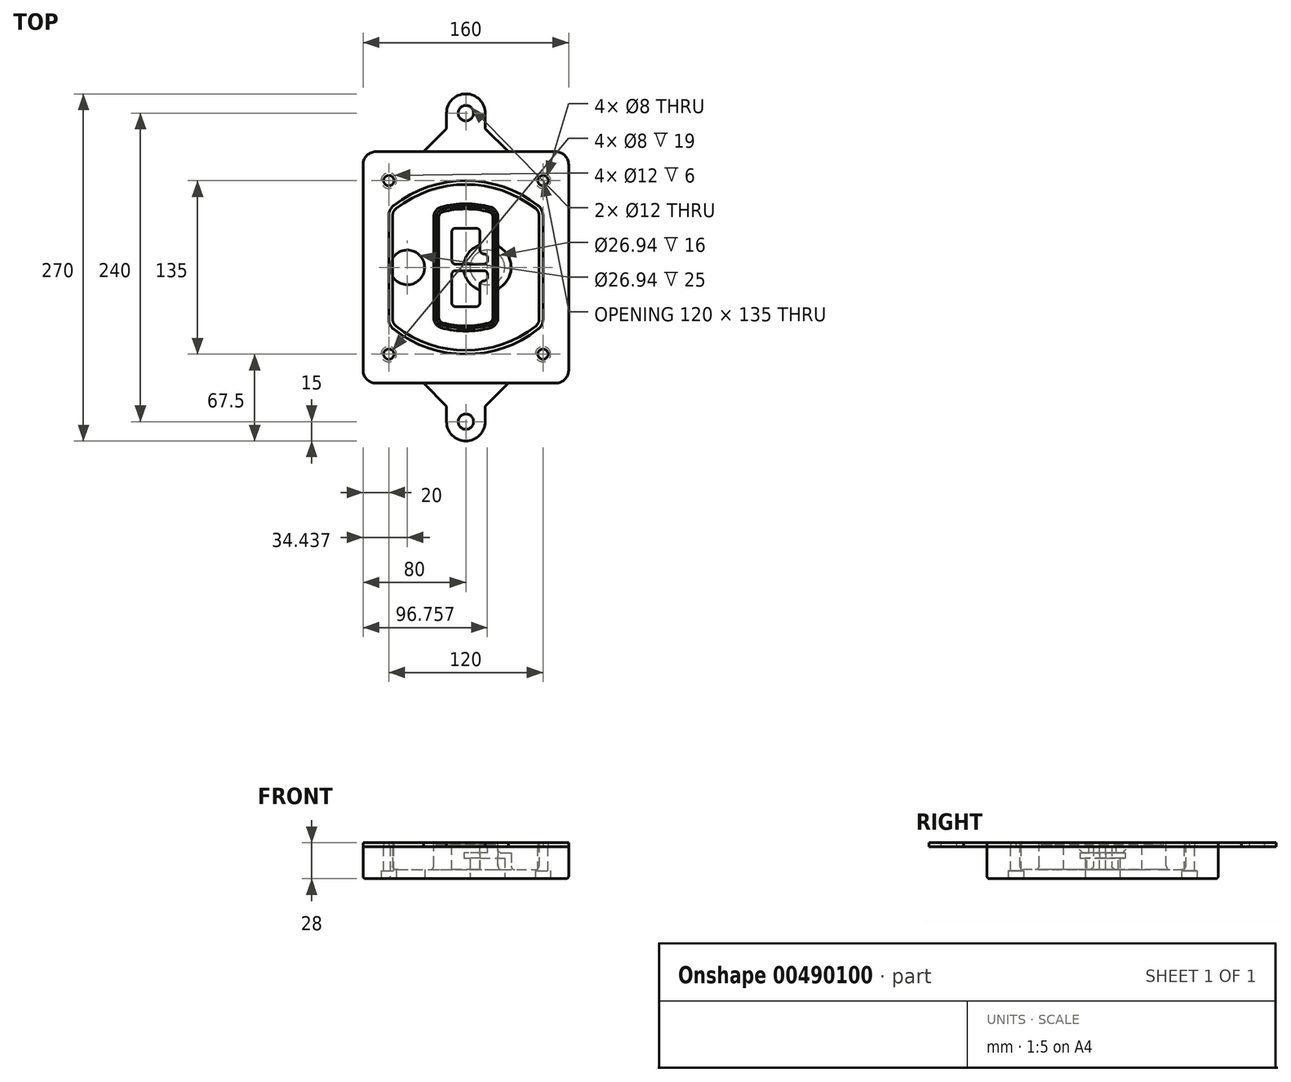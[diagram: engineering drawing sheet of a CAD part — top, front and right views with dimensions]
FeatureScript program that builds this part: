
annotation { "Feature Type Name" : "Feature", "Feature Type Description" : "" }
export const myFeature = defineFeature(function(context is Context, id is Id, definition is map)
    precondition{}
    {
        {
            var Q0;
            Q0=qCreatedBy(makeId("Top.planeOp"),FACE);
            var sketch = newSketch(context, id + "F0", { "sketchPlane" : qUnion([Q0])});
            skPoint(sketch, "E0.rect.middle", {"position": v(0, 0) * mm});
            skLineSegment(sketch, "E1.bottom", {"start": v(-70, -90) * mm, "end": v(70, -90) * mm});
            skLineSegment(sketch, "E1.top", {"start": v(-70, 90) * mm, "end": v(70, 90) * mm});
            skLineSegment(sketch, "E1.left", {"start": v(-80, -80) * mm, "end": v(-80, 80) * mm});
            skLineSegment(sketch, "E1.right", {"start": v(80, -80) * mm, "end": v(80, 80) * mm});
            skLineSegment(sketch, "E2", {"start": v(-80, 90) * mm, "end": v(80, -90) * mm, "construction": true});
            skLineSegment(sketch, "E3", {"start": v(80, 90) * mm, "end": v(-80, -90) * mm, "construction": true});
            skCircle(sketch, "E4", {"center": v(-60, 67.5) * mm, "radius": 4 * mm});
            skCircle(sketch, "E5", {"center": v(60, 67.5) * mm, "radius": 4 * mm});
            skCircle(sketch, "E6", {"center": v(60, -67.5) * mm, "radius": 4 * mm});
            skCircle(sketch, "E7", {"center": v(-60, -67.5) * mm, "radius": 4 * mm});
            skLineSegment(sketch, "E8", {"start": v(-60, 67.5) * mm, "end": v(60, 67.5) * mm, "construction": true});
            skLineSegment(sketch, "E9", {"start": v(60, 67.5) * mm, "end": v(60, -67.5) * mm, "construction": true});
            skLineSegment(sketch, "E10", {"start": v(60, -67.5) * mm, "end": v(-60, -67.5) * mm, "construction": true});
            skLineSegment(sketch, "E11", {"start": v(-60, -67.5) * mm, "end": v(-60, 67.5) * mm, "construction": true});
            skLineSegment(sketch, "E12", {"start": v(-60, 40.3) * mm, "end": v(-60, -40.3) * mm});
            skLineSegment(sketch, "E13", {"start": v(60, 40.3) * mm, "end": v(60, -40.3) * mm});
            skArc(sketch, "E14", {"start": v(56.15, 48.18) * mm, "mid": v(0, 67.5) * mm, "end": v(-56.15, 48.18) * mm});
            skArc(sketch, "E15", {"start": v(-56.15, -48.18) * mm, "mid": v(0, -67.5) * mm, "end": v(56.15, -48.18) * mm});
            skLineSegment(sketch, "E16", {"start": v(-60, 0) * mm, "end": v(60, 0) * mm, "construction": true});
            skPoint(sketch, "E17.visualSharp", {"position": v(-60, -45) * mm});
            skArc(sketch, "E17.filletArc", {"start": v(-60, -40.3) * mm, "mid": v(-58.99, -44.68) * mm, "end": v(-56.15, -48.18) * mm});
            skPoint(sketch, "E18.visualSharp", {"position": v(-60, 45) * mm});
            skArc(sketch, "E18.filletArc", {"start": v(-56.15, 48.18) * mm, "mid": v(-58.99, 44.68) * mm, "end": v(-60, 40.3) * mm});
            skPoint(sketch, "E19.visualSharp", {"position": v(60, 45) * mm});
            skArc(sketch, "E19.filletArc", {"start": v(60, 40.3) * mm, "mid": v(58.99, 44.68) * mm, "end": v(56.15, 48.18) * mm});
            skPoint(sketch, "E20.visualSharp", {"position": v(60, -45) * mm});
            skArc(sketch, "E20.filletArc", {"start": v(56.15, -48.18) * mm, "mid": v(58.99, -44.68) * mm, "end": v(60, -40.3) * mm});
            skPoint(sketch, "E21.visualSharp", {"position": v(-80, 90) * mm});
            skArc(sketch, "E21.filletArc", {"start": v(-70, 90) * mm, "mid": v(-77.07, 87.07) * mm, "end": v(-80, 80) * mm});
            skPoint(sketch, "E22.visualSharp", {"position": v(80, 90) * mm});
            skArc(sketch, "E22.filletArc", {"start": v(80, 80) * mm, "mid": v(77.07, 87.07) * mm, "end": v(70, 90) * mm});
            skPoint(sketch, "E23.visualSharp", {"position": v(80, -90) * mm});
            skArc(sketch, "E23.filletArc", {"start": v(70, -90) * mm, "mid": v(77.07, -87.07) * mm, "end": v(80, -80) * mm});
            skPoint(sketch, "E24.visualSharp", {"position": v(-80, -90) * mm});
            skArc(sketch, "E24.filletArc", {"start": v(-80, -80) * mm, "mid": v(-77.07, -87.07) * mm, "end": v(-70, -90) * mm});
            skArc(sketch, "E25.0", {"start": v(57, 40.3) * mm, "mid": v(56.3, 43.36) * mm, "end": v(54.3, 45.81) * mm});
            skLineSegment(sketch, "E25.1", {"start": v(57, 40.3) * mm, "end": v(57, -40.3) * mm});
            skArc(sketch, "E25.2", {"start": v(54.3, -45.81) * mm, "mid": v(56.3, -43.36) * mm, "end": v(57, -40.3) * mm});
            skArc(sketch, "E25.3", {"start": v(-54.3, -45.81) * mm, "mid": v(0, -64.5) * mm, "end": v(54.3, -45.81) * mm});
            skArc(sketch, "E25.4", {"start": v(-57, -40.3) * mm, "mid": v(-56.3, -43.36) * mm, "end": v(-54.3, -45.81) * mm});
            skArc(sketch, "E25.5", {"start": v(54.3, 45.81) * mm, "mid": v(0, 64.5) * mm, "end": v(-54.3, 45.81) * mm});
            skLineSegment(sketch, "E25.6", {"start": v(-57, 40.3) * mm, "end": v(-57, -40.3) * mm});
            skArc(sketch, "E25.7", {"start": v(-54.3, 45.81) * mm, "mid": v(-56.3, 43.36) * mm, "end": v(-57, 40.3) * mm});
            skArc(sketch, "E26.0", {"start": v(-58.62, 51.33) * mm, "mid": v(-62.58, 46.43) * mm, "end": v(-64, 40.3) * mm});
            skArc(sketch, "E26.1", {"start": v(58.62, 51.33) * mm, "mid": v(0, 71.5) * mm, "end": v(-58.62, 51.33) * mm});
            skArc(sketch, "E26.2", {"start": v(64, 40.3) * mm, "mid": v(62.58, 46.43) * mm, "end": v(58.62, 51.33) * mm});
            skLineSegment(sketch, "E26.3", {"start": v(64, 40.3) * mm, "end": v(64, -40.3) * mm});
            skArc(sketch, "E26.4", {"start": v(58.62, -51.33) * mm, "mid": v(62.58, -46.43) * mm, "end": v(64, -40.3) * mm});
            skLineSegment(sketch, "E26.5", {"start": v(-64, 40.3) * mm, "end": v(-64, -40.3) * mm});
            skArc(sketch, "E26.6", {"start": v(-58.62, -51.33) * mm, "mid": v(0, -71.5) * mm, "end": v(58.62, -51.33) * mm});
            skArc(sketch, "E26.7", {"start": v(-64, -40.3) * mm, "mid": v(-62.58, -46.43) * mm, "end": v(-58.62, -51.33) * mm});
            skSolve(sketch);
        }
        {
            var Q0;
            Q0=makeQuery(id+"F0.imprint","IMPRINT",FACE,{"disambiguationData":[TD([[makeQuery(id+"F0.imprint","IMPRINT",EDGE,{"derivedFrom":sQuery(id+"F0.wireOp",EDGE,"E1.bottom")}),1.0]])]});
            var Q1;
            Q1=makeQuery(id+"F0.imprint","IMPRINT",FACE,{"disambiguationData":[TD([[makeQuery(id+"F0.imprint","IMPRINT",EDGE,{"derivedFrom":sQuery(id+"F0.wireOp",EDGE,"E12")}),1.0]])]});
            var Q2;
            Q2=makeQuery(id+"F0.imprint","IMPRINT",FACE,{"disambiguationData":[TD([[makeQuery(id+"F0.imprint","IMPRINT",EDGE,{"derivedFrom":sQuery(id+"F0.wireOp",EDGE,"E25.0")}),1.0]])]});
            var Q3;
            Q3=makeQuery(id+"F0.imprint","IMPRINT",FACE,{"disambiguationData":[TD([[makeQuery(id+"F0.imprint","IMPRINT",EDGE,{"derivedFrom":sQuery(id+"F0.wireOp",EDGE,"E12")}),-1.0]])]});
            extrude(context, id + "F1", {"entities" : qUnion([Q0, Q1, Q2, Q3]), "oppositeDirection" : true, "depth" : 25 * mm});
        }
        {
            var Q0;
            Q0=makeQuery(id+"F0.imprint","IMPRINT",FACE,{"disambiguationData":[TD([[makeQuery(id+"F0.imprint","IMPRINT",EDGE,{"derivedFrom":sQuery(id+"F0.wireOp",EDGE,"E12")}),1.0]])]});
            extrude(context, id + "F2", {"entities" : qUnion([Q0]), "operationType" : NewBodyOperationType.ADD, "depth" : 3 * mm});
        }
        {
            var Q0;
            Q0=makeQuery(id+"F0.imprint","IMPRINT",FACE,{"disambiguationData":[TD([[makeQuery(id+"F0.imprint","IMPRINT",EDGE,{"derivedFrom":sQuery(id+"F0.wireOp",EDGE,"E25.0")}),1.0]])]});
            extrude(context, id + "F3", {"entities" : qUnion([Q0]), "operationType" : NewBodyOperationType.REMOVE, "oppositeDirection" : true, "depth" : 18 * mm});
        }
        {
            var Q0;
            Q0=makeQuery(id+"F2.opExtrude","CAP_FACE",FACE,{"disambiguationData":[OSD([sQuery(id+"F0.wireOp",EDGE,"E12"),sQuery(id+"F0.wireOp",EDGE,"E13"),sQuery(id+"F0.wireOp",EDGE,"E14"),sQuery(id+"F0.wireOp",EDGE,"E15"),sQuery(id+"F0.wireOp",EDGE,"E17.filletArc"),sQuery(id+"F0.wireOp",EDGE,"E18.filletArc"),sQuery(id+"F0.wireOp",EDGE,"E19.filletArc"),sQuery(id+"F0.wireOp",EDGE,"E20.filletArc"),sQuery(id+"F0.wireOp",EDGE,"E25.0"),sQuery(id+"F0.wireOp",EDGE,"E25.1"),sQuery(id+"F0.wireOp",EDGE,"E25.2"),sQuery(id+"F0.wireOp",EDGE,"E25.3"),sQuery(id+"F0.wireOp",EDGE,"E25.4"),sQuery(id+"F0.wireOp",EDGE,"E25.5"),sQuery(id+"F0.wireOp",EDGE,"E25.6"),sQuery(id+"F0.wireOp",EDGE,"E25.7")])],"isStart":false});
            var sketch = newSketch(context, id + "F4", { "sketchPlane" : qUnion([Q0])});
            skArc(sketch, "E27.0", {"start": v(-19.08, -46.97) * mm, "mid": v(0, -49.5) * mm, "end": v(19.08, -46.97) * mm});
            skArc(sketch, "E28.0", {"start": v(19.08, 46.97) * mm, "mid": v(0, 49.5) * mm, "end": v(-19.08, 46.97) * mm});
            skLineSegment(sketch, "E29", {"start": v(-25, 39.25) * mm, "end": v(-25, -39.25) * mm});
            skLineSegment(sketch, "E30", {"start": v(25, 39.25) * mm, "end": v(25, -39.25) * mm});
            skLineSegment(sketch, "E31", {"start": v(-25, 45.1) * mm, "end": v(25, 45.1) * mm, "construction": true});
            skLineSegment(sketch, "E32", {"start": v(-25, -45.1) * mm, "end": v(25, -45.1) * mm, "construction": true});
            skPoint(sketch, "E33.visualSharp", {"position": v(-25, 45.1) * mm});
            skArc(sketch, "E33.filletArc", {"start": v(-19.08, 46.97) * mm, "mid": v(-23.35, 44.11) * mm, "end": v(-25, 39.25) * mm});
            skPoint(sketch, "E34.visualSharp", {"position": v(25, 45.1) * mm});
            skArc(sketch, "E34.filletArc", {"start": v(25, 39.25) * mm, "mid": v(23.35, 44.11) * mm, "end": v(19.08, 46.97) * mm});
            skPoint(sketch, "E35.visualSharp", {"position": v(25, -45.1) * mm});
            skArc(sketch, "E35.filletArc", {"start": v(19.08, -46.97) * mm, "mid": v(23.35, -44.11) * mm, "end": v(25, -39.25) * mm});
            skPoint(sketch, "E36.visualSharp", {"position": v(-25, -45.1) * mm});
            skArc(sketch, "E36.filletArc", {"start": v(-25, -39.25) * mm, "mid": v(-23.35, -44.11) * mm, "end": v(-19.08, -46.97) * mm});
            skArc(sketch, "E37.0", {"start": v(54.3, 45.81) * mm, "mid": v(0, 64.5) * mm, "end": v(-54.3, 45.81) * mm});
            skArc(sketch, "E37.1", {"start": v(-54.3, 45.81) * mm, "mid": v(-56.3, 43.36) * mm, "end": v(-57, 40.3) * mm});
            skLineSegment(sketch, "E37.2", {"start": v(-57, 40.3) * mm, "end": v(-57, -40.3) * mm});
            skArc(sketch, "E37.3", {"start": v(-57, -40.3) * mm, "mid": v(-56.3, -43.36) * mm, "end": v(-54.3, -45.81) * mm});
            skArc(sketch, "E37.4", {"start": v(-54.3, -45.81) * mm, "mid": v(0, -64.5) * mm, "end": v(54.3, -45.81) * mm});
            skArc(sketch, "E37.5", {"start": v(54.3, -45.81) * mm, "mid": v(56.3, -43.36) * mm, "end": v(57, -40.3) * mm});
            skLineSegment(sketch, "E37.6", {"start": v(57, 40.3) * mm, "end": v(57, -40.3) * mm});
            skArc(sketch, "E37.7", {"start": v(57, 40.3) * mm, "mid": v(56.3, 43.36) * mm, "end": v(54.3, 45.81) * mm});
            skLineSegment(sketch, "E38.0", {"start": v(23, 39.25) * mm, "end": v(23, -39.25) * mm});
            skArc(sketch, "E38.1", {"start": v(18.56, -45.04) * mm, "mid": v(21.76, -42.9) * mm, "end": v(23, -39.25) * mm});
            skArc(sketch, "E38.2", {"start": v(-18.56, -45.04) * mm, "mid": v(0, -47.5) * mm, "end": v(18.56, -45.04) * mm});
            skArc(sketch, "E38.3", {"start": v(-23, -39.25) * mm, "mid": v(-21.76, -42.9) * mm, "end": v(-18.56, -45.04) * mm});
            skLineSegment(sketch, "E38.4", {"start": v(-23, 39.25) * mm, "end": v(-23, -39.25) * mm});
            skArc(sketch, "E38.5", {"start": v(23, 39.25) * mm, "mid": v(21.76, 42.9) * mm, "end": v(18.56, 45.04) * mm});
            skArc(sketch, "E38.6", {"start": v(-18.56, 45.04) * mm, "mid": v(-21.76, 42.9) * mm, "end": v(-23, 39.25) * mm});
            skArc(sketch, "E38.7", {"start": v(18.56, 45.04) * mm, "mid": v(0, 47.5) * mm, "end": v(-18.56, 45.04) * mm});
            skArc(sketch, "E39.0", {"start": v(21, 39.25) * mm, "mid": v(20.18, 41.68) * mm, "end": v(18.04, 43.1) * mm});
            skLineSegment(sketch, "E39.1", {"start": v(21, 39.25) * mm, "end": v(21, -39.25) * mm});
            skArc(sketch, "E39.2", {"start": v(18.04, -43.1) * mm, "mid": v(20.18, -41.68) * mm, "end": v(21, -39.25) * mm});
            skArc(sketch, "E39.3", {"start": v(-18.04, -43.1) * mm, "mid": v(0, -45.5) * mm, "end": v(18.04, -43.1) * mm});
            skArc(sketch, "E39.4", {"start": v(-21, -39.25) * mm, "mid": v(-20.18, -41.68) * mm, "end": v(-18.04, -43.1) * mm});
            skArc(sketch, "E39.5", {"start": v(18.04, 43.1) * mm, "mid": v(0, 45.5) * mm, "end": v(-18.04, 43.1) * mm});
            skLineSegment(sketch, "E39.6", {"start": v(-21, 39.25) * mm, "end": v(-21, -39.25) * mm});
            skArc(sketch, "E39.7", {"start": v(-18.04, 43.1) * mm, "mid": v(-20.18, 41.68) * mm, "end": v(-21, 39.25) * mm});
            skLineSegment(sketch, "E40", {"start": v(-25, 0) * mm, "end": v(25, 0) * mm, "construction": true});
            skLineSegment(sketch, "E41", {"start": v(-11, 5.5) * mm, "end": v(-11, 27.5) * mm});
            skLineSegment(sketch, "E42", {"start": v(-8, 30.5) * mm, "end": v(8, 30.5) * mm});
            skLineSegment(sketch, "E43", {"start": v(11, 27.5) * mm, "end": v(11, 13.5) * mm});
            skLineSegment(sketch, "E44", {"start": v(14, 10.5) * mm, "end": v(14, 10.5) * mm});
            skLineSegment(sketch, "E45", {"start": v(17, 7.5) * mm, "end": v(17, 5.5) * mm});
            skLineSegment(sketch, "E46", {"start": v(14, 2.5) * mm, "end": v(-8, 2.5) * mm});
            skPoint(sketch, "E47.visualSharp", {"position": v(-11, 30.5) * mm});
            skArc(sketch, "E47.filletArc", {"start": v(-8, 30.5) * mm, "mid": v(-10.12, 29.62) * mm, "end": v(-11, 27.5) * mm});
            skPoint(sketch, "E48.visualSharp", {"position": v(11, 30.5) * mm});
            skArc(sketch, "E48.filletArc", {"start": v(11, 27.5) * mm, "mid": v(10.12, 29.62) * mm, "end": v(8, 30.5) * mm});
            skPoint(sketch, "E49.visualSharp", {"position": v(11, 10.5) * mm});
            skArc(sketch, "E49.filletArc", {"start": v(11, 13.5) * mm, "mid": v(11.88, 11.38) * mm, "end": v(14, 10.5) * mm});
            skPoint(sketch, "E50.visualSharp", {"position": v(17, 10.5) * mm});
            skArc(sketch, "E50.filletArc", {"start": v(17, 7.5) * mm, "mid": v(16.12, 9.62) * mm, "end": v(14, 10.5) * mm});
            skPoint(sketch, "E51.visualSharp", {"position": v(17, 2.5) * mm});
            skArc(sketch, "E51.filletArc", {"start": v(14, 2.5) * mm, "mid": v(16.12, 3.38) * mm, "end": v(17, 5.5) * mm});
            skPoint(sketch, "E52.visualSharp", {"position": v(-11, 2.5) * mm});
            skArc(sketch, "E52.filletArc", {"start": v(-11, 5.5) * mm, "mid": v(-10.12, 3.38) * mm, "end": v(-8, 2.5) * mm});
            skLineSegment(sketch, "E53.0.MirrorCS", {"start": v(14, -2.5) * mm, "end": v(-8, -2.5) * mm});
            skArc(sketch, "E54.0.MirrorCS", {"start": v(-11, -5.5) * mm, "mid": v(-10.12, -3.38) * mm, "end": v(-8, -2.5) * mm});
            skLineSegment(sketch, "E55.0.MirrorCS", {"start": v(-11, -5.5) * mm, "end": v(-11, -27.5) * mm});
            skArc(sketch, "E56.0.MirrorCS", {"start": v(-8, -30.5) * mm, "mid": v(-10.12, -29.62) * mm, "end": v(-11, -27.5) * mm});
            skLineSegment(sketch, "E57.0.MirrorCS", {"start": v(-8, -30.5) * mm, "end": v(8, -30.5) * mm});
            skArc(sketch, "E58.0.MirrorCS", {"start": v(11, -27.5) * mm, "mid": v(10.12, -29.62) * mm, "end": v(8, -30.5) * mm});
            skLineSegment(sketch, "E59.0.MirrorCS", {"start": v(11, -27.5) * mm, "end": v(11, -13.5) * mm});
            skArc(sketch, "E60.0.MirrorCS", {"start": v(11, -13.5) * mm, "mid": v(11.88, -11.38) * mm, "end": v(14, -10.5) * mm});
            skArc(sketch, "E61.0.MirrorCS", {"start": v(17, -7.5) * mm, "mid": v(16.12, -9.62) * mm, "end": v(14, -10.5) * mm});
            skLineSegment(sketch, "E62.0.MirrorCS", {"start": v(17, -7.5) * mm, "end": v(17, -5.5) * mm});
            skArc(sketch, "E63.0.MirrorCS", {"start": v(14, -2.5) * mm, "mid": v(16.12, -3.38) * mm, "end": v(17, -5.5) * mm});
            skSolve(sketch);
        }
        {
            var Q0;
            Q0=makeQuery(id+"F4.imprint","IMPRINT",FACE,{"disambiguationData":[TD([[makeQuery(id+"F4.imprint","IMPRINT",EDGE,{"derivedFrom":sQuery(id+"F4.wireOp",EDGE,"E27.0")}),1.0]])]});
            var Q1;
            Q1=makeQuery(id+"F4.imprint","IMPRINT",FACE,{"disambiguationData":[TD([[makeQuery(id+"F4.imprint","IMPRINT",EDGE,{"derivedFrom":sQuery(id+"F4.wireOp",EDGE,"E38.0")}),-1.0]])]});
            var Q2;
            Q2=makeQuery(id+"F4.imprint","IMPRINT",FACE,{"disambiguationData":[TD([[makeQuery(id+"F4.imprint","IMPRINT",EDGE,{"derivedFrom":sQuery(id+"F4.wireOp",EDGE,"E39.0")}),1.0]])]});
            extrude(context, id + "F5", {"entities" : qUnion([Q0, Q1, Q2]), "operationType" : NewBodyOperationType.ADD, "endBound" : BoundingType.UP_TO_NEXT, "oppositeDirection" : true, "depth" : 25 * mm});
        }
        {
            var Q0;
            Q0=makeQuery(id+"F4.imprint","IMPRINT",FACE,{"disambiguationData":[TD([[makeQuery(id+"F4.imprint","IMPRINT",EDGE,{"derivedFrom":sQuery(id+"F4.wireOp",EDGE,"E38.0")}),-1.0]])]});
            extrude(context, id + "F6", {"entities" : qUnion([Q0]), "operationType" : NewBodyOperationType.REMOVE, "oppositeDirection" : true, "depth" : 2 * mm});
        }
        {
            var Q0;
            Q0=makeQuery(id+"F1.opExtrude","CAP_FACE",FACE,{"disambiguationData":[OSD([sQuery(id+"F0.wireOp",EDGE,"E1.bottom"),sQuery(id+"F0.wireOp",EDGE,"E1.top"),sQuery(id+"F0.wireOp",EDGE,"E1.left"),sQuery(id+"F0.wireOp",EDGE,"E1.right"),sQuery(id+"F0.wireOp",EDGE,"E4"),sQuery(id+"F0.wireOp",EDGE,"E5"),sQuery(id+"F0.wireOp",EDGE,"E6"),sQuery(id+"F0.wireOp",EDGE,"E7"),sQuery(id+"F0.wireOp",EDGE,"E21.filletArc"),sQuery(id+"F0.wireOp",EDGE,"E22.filletArc"),sQuery(id+"F0.wireOp",EDGE,"E23.filletArc"),sQuery(id+"F0.wireOp",EDGE,"E24.filletArc")])],"isStart":false});
            var sketch = newSketch(context, id + "F7", { "sketchPlane" : qUnion([Q0])});
            skCircle(sketch, "E64", {"center": v(16.76, 0) * mm, "radius": 13.47 * mm});
            skCircle(sketch, "E65", {"center": v(-45.56, 0) * mm, "radius": 13.47 * mm});
            skLineSegment(sketch, "E66", {"start": v(80, 0) * mm, "end": v(-80, 0) * mm});
            skCircle(sketch, "E67", {"center": v(16.76, 0) * mm, "radius": 18.47 * mm});
            skCircle(sketch, "E68", {"center": v(60, -67.5) * mm, "radius": 6 * mm});
            skCircle(sketch, "E69", {"center": v(-60, -67.5) * mm, "radius": 6 * mm});
            skCircle(sketch, "E70", {"center": v(-60, 67.5) * mm, "radius": 6 * mm});
            skCircle(sketch, "E71", {"center": v(60, 67.5) * mm, "radius": 6 * mm});
            skSolve(sketch);
        }
        {
            var Q0;
            {var subQ1=sQuery(id+"F7.wireOp",EDGE,"E66");var subQ4=sQuery(id+"F7.wireOp",EDGE,"E64");var subQ6=makeQuery(id+"F7.imprint","INTERSECT",VERTEX,{"disambiguationData":[OD(0.0)],"derivedFrom":[subQ4,subQ1]});Q0=makeQuery(id+"F7.imprint","IMPRINT",FACE,{"disambiguationData":[TD([[makeQuery(id+"F7.imprint","IMPRINT",EDGE,{"disambiguationData":[TD([[subQ6,-1.0]])],"derivedFrom":subQ4}),-1.0]])]});}
            var Q1;
            {var subQ0=sQuery(id+"F7.wireOp",EDGE,"E66");var subQ1=sQuery(id+"F7.wireOp",EDGE,"E64");var subQ3=makeQuery(id+"F7.imprint","INTERSECT",VERTEX,{"disambiguationData":[OD(0.0)],"derivedFrom":[subQ1,subQ0]});Q1=makeQuery(id+"F7.imprint","IMPRINT",FACE,{"disambiguationData":[TD([[makeQuery(id+"F7.imprint","IMPRINT",EDGE,{"disambiguationData":[TD([[subQ3,-1.0]])],"derivedFrom":subQ1}),1.0]])]});}
            var Q2;
            {var subQ0=sQuery(id+"F7.wireOp",EDGE,"E66");var subQ1=sQuery(id+"F7.wireOp",EDGE,"E64");var subQ3=makeQuery(id+"F7.imprint","INTERSECT",VERTEX,{"disambiguationData":[OD(0.0)],"derivedFrom":[subQ1,subQ0]});Q2=makeQuery(id+"F7.imprint","IMPRINT",FACE,{"disambiguationData":[TD([[makeQuery(id+"F7.imprint","IMPRINT",EDGE,{"disambiguationData":[TD([[subQ3,1.0]])],"derivedFrom":subQ1}),1.0]])]});}
            var Q3;
            {var subQ1=sQuery(id+"F7.wireOp",EDGE,"E66");var subQ4=sQuery(id+"F7.wireOp",EDGE,"E64");var subQ6=makeQuery(id+"F7.imprint","INTERSECT",VERTEX,{"disambiguationData":[OD(0.0)],"derivedFrom":[subQ4,subQ1]});Q3=makeQuery(id+"F7.imprint","IMPRINT",FACE,{"disambiguationData":[TD([[makeQuery(id+"F7.imprint","IMPRINT",EDGE,{"disambiguationData":[TD([[subQ6,1.0]])],"derivedFrom":subQ4}),-1.0]])]});}
            extrude(context, id + "F8", {"entities" : qUnion([Q0, Q1, Q2, Q3]), "operationType" : NewBodyOperationType.ADD, "oppositeDirection" : true, "depth" : 20 * mm});
        }
        {
            var Q0;
            {var subQ0=sQuery(id+"F7.wireOp",EDGE,"E66");var subQ1=sQuery(id+"F7.wireOp",EDGE,"E64");var subQ3=makeQuery(id+"F7.imprint","INTERSECT",VERTEX,{"disambiguationData":[OD(0.0)],"derivedFrom":[subQ1,subQ0]});Q0=makeQuery(id+"F7.imprint","IMPRINT",FACE,{"disambiguationData":[TD([[makeQuery(id+"F7.imprint","IMPRINT",EDGE,{"disambiguationData":[TD([[subQ3,-1.0]])],"derivedFrom":subQ1}),1.0]])]});}
            var Q1;
            {var subQ0=sQuery(id+"F7.wireOp",EDGE,"E66");var subQ1=sQuery(id+"F7.wireOp",EDGE,"E64");var subQ3=makeQuery(id+"F7.imprint","INTERSECT",VERTEX,{"disambiguationData":[OD(0.0)],"derivedFrom":[subQ1,subQ0]});Q1=makeQuery(id+"F7.imprint","IMPRINT",FACE,{"disambiguationData":[TD([[makeQuery(id+"F7.imprint","IMPRINT",EDGE,{"disambiguationData":[TD([[subQ3,1.0]])],"derivedFrom":subQ1}),1.0]])]});}
            extrude(context, id + "F9", {"entities" : qUnion([Q0, Q1]), "operationType" : NewBodyOperationType.REMOVE, "oppositeDirection" : true, "depth" : 16 * mm});
        }
        {
            var Q0;
            {var subQ0=sQuery(id+"F7.wireOp",EDGE,"E66");var subQ1=sQuery(id+"F7.wireOp",EDGE,"E65");var subQ3=makeQuery(id+"F7.imprint","INTERSECT",VERTEX,{"disambiguationData":[OD(0.0)],"derivedFrom":[subQ1,subQ0]});Q0=makeQuery(id+"F7.imprint","IMPRINT",FACE,{"disambiguationData":[TD([[makeQuery(id+"F7.imprint","IMPRINT",EDGE,{"disambiguationData":[TD([[subQ3,-1.0]])],"derivedFrom":subQ1}),1.0]])]});}
            var Q1;
            {var subQ0=sQuery(id+"F7.wireOp",EDGE,"E66");var subQ1=sQuery(id+"F7.wireOp",EDGE,"E65");var subQ3=makeQuery(id+"F7.imprint","INTERSECT",VERTEX,{"disambiguationData":[OD(0.0)],"derivedFrom":[subQ1,subQ0]});Q1=makeQuery(id+"F7.imprint","IMPRINT",FACE,{"disambiguationData":[TD([[makeQuery(id+"F7.imprint","IMPRINT",EDGE,{"disambiguationData":[TD([[subQ3,1.0]])],"derivedFrom":subQ1}),1.0]])]});}
            extrude(context, id + "F10", {"entities" : qUnion([Q0, Q1]), "operationType" : NewBodyOperationType.REMOVE, "oppositeDirection" : true, "depth" : 25 * mm});
        }
        {
            var Q0;
            Q0=makeQuery(id+"F7.imprint","IMPRINT",FACE,{"disambiguationData":[TD([[makeQuery(id+"F7.imprint","IMPRINT",EDGE,{"derivedFrom":sQuery(id+"F7.wireOp",EDGE,"E68")}),1.0]])]});
            var Q1;
            Q1=makeQuery(id+"F7.imprint","IMPRINT",FACE,{"disambiguationData":[TD([[makeQuery(id+"F7.imprint","IMPRINT",EDGE,{"derivedFrom":makeQuery(id+"F1.opExtrude","CAP_EDGE",EDGE,{"disambiguationData":[OSD([sQuery(id+"F0.wireOp",EDGE,"E5")])],"isStart":false})}),-1.0]])]});
            var Q2;
            Q2=makeQuery(id+"F7.imprint","IMPRINT",FACE,{"disambiguationData":[TD([[makeQuery(id+"F7.imprint","IMPRINT",EDGE,{"derivedFrom":sQuery(id+"F7.wireOp",EDGE,"E69")}),1.0]])]});
            var Q3;
            Q3=makeQuery(id+"F7.imprint","IMPRINT",FACE,{"disambiguationData":[TD([[makeQuery(id+"F7.imprint","IMPRINT",EDGE,{"derivedFrom":makeQuery(id+"F1.opExtrude","CAP_EDGE",EDGE,{"disambiguationData":[OSD([sQuery(id+"F0.wireOp",EDGE,"E4")])],"isStart":false})}),-1.0]])]});
            var Q4;
            Q4=makeQuery(id+"F7.imprint","IMPRINT",FACE,{"disambiguationData":[TD([[makeQuery(id+"F7.imprint","IMPRINT",EDGE,{"derivedFrom":sQuery(id+"F7.wireOp",EDGE,"E70")}),1.0]])]});
            var Q5;
            Q5=makeQuery(id+"F7.imprint","IMPRINT",FACE,{"disambiguationData":[TD([[makeQuery(id+"F7.imprint","IMPRINT",EDGE,{"derivedFrom":makeQuery(id+"F1.opExtrude","CAP_EDGE",EDGE,{"disambiguationData":[OSD([sQuery(id+"F0.wireOp",EDGE,"E7")])],"isStart":false})}),-1.0]])]});
            var Q6;
            Q6=makeQuery(id+"F7.imprint","IMPRINT",FACE,{"disambiguationData":[TD([[makeQuery(id+"F7.imprint","IMPRINT",EDGE,{"derivedFrom":sQuery(id+"F7.wireOp",EDGE,"E71")}),1.0]])]});
            var Q7;
            Q7=makeQuery(id+"F7.imprint","IMPRINT",FACE,{"disambiguationData":[TD([[makeQuery(id+"F7.imprint","IMPRINT",EDGE,{"derivedFrom":makeQuery(id+"F1.opExtrude","CAP_EDGE",EDGE,{"disambiguationData":[OSD([sQuery(id+"F0.wireOp",EDGE,"E6")])],"isStart":false})}),-1.0]])]});
            extrude(context, id + "F11", {"entities" : qUnion([Q0, Q1, Q2, Q3, Q4, Q5, Q6, Q7]), "operationType" : NewBodyOperationType.REMOVE, "oppositeDirection" : true, "depth" : 6 * mm});
        }
        {
            var Q0;
            Q0=makeQuery(id+"F9.boolean.opBoolean","COPY",FACE,{"derivedFrom":makeQuery(id+"F9.opExtrude","CAP_FACE",FACE,{"disambiguationData":[OSD([sQuery(id+"F7.wireOp",EDGE,"E64")])],"isStart":false})});
            var sketch = newSketch(context, id + "F12", { "sketchPlane" : qUnion([Q0])});
            skArc(sketch, "E72.0", {"start": v(11, 17.55) * mm, "mid": v(2.57, 11.82) * mm, "end": v(-1.54, 2.5) * mm});
            skArc(sketch, "E72.1", {"start": v(-1.54, -2.5) * mm, "mid": v(2.57, -11.82) * mm, "end": v(11, -17.55) * mm});
            skLineSegment(sketch, "E73", {"start": v(-1.54, -2.5) * mm, "end": v(14, -2.5) * mm});
            skLineSegment(sketch, "E74.0", {"start": v(14, 2.5) * mm, "end": v(-1.54, 2.5) * mm});
            skArc(sketch, "E74.1", {"start": v(14, 2.5) * mm, "mid": v(16.12, 3.38) * mm, "end": v(17, 5.5) * mm});
            skLineSegment(sketch, "E74.2", {"start": v(17, 7.5) * mm, "end": v(17, 5.5) * mm});
            skArc(sketch, "E74.3", {"start": v(17, 7.5) * mm, "mid": v(16.12, 9.62) * mm, "end": v(14, 10.5) * mm});
            skArc(sketch, "E74.4", {"start": v(11, 13.5) * mm, "mid": v(11.88, 11.38) * mm, "end": v(14, 10.5) * mm});
            skLineSegment(sketch, "E74.5", {"start": v(11, 17.55) * mm, "end": v(11, 13.5) * mm});
            skLineSegment(sketch, "E74.7", {"start": v(14, -2.5) * mm, "end": v(-1.54, -2.5) * mm});
            skArc(sketch, "E74.8", {"start": v(14, -2.5) * mm, "mid": v(16.12, -3.38) * mm, "end": v(17, -5.5) * mm});
            skLineSegment(sketch, "E74.9", {"start": v(17, -7.5) * mm, "end": v(17, -5.5) * mm});
            skArc(sketch, "E74.10", {"start": v(17, -7.5) * mm, "mid": v(16.12, -9.62) * mm, "end": v(14, -10.5) * mm});
            skArc(sketch, "E74.11", {"start": v(11, -13.5) * mm, "mid": v(11.88, -11.38) * mm, "end": v(14, -10.5) * mm});
            skLineSegment(sketch, "E74.12", {"start": v(11, -17.55) * mm, "end": v(11, -13.5) * mm});
            skPoint(sketch, "E75.orphan", {"position": v(11, -27.5) * mm});
            skPoint(sketch, "E76.orphan", {"position": v(-8, -2.5) * mm});
            skPoint(sketch, "E77.orphan", {"position": v(-8, 2.5) * mm});
            skPoint(sketch, "E78.orphan", {"position": v(11, 27.5) * mm});
            skSolve(sketch);
        }
        {
            var Q0;
            {var subQ7=sQuery(id+"F12.wireOp",EDGE,"E72.0");var subQ14=sQuery(id+"F12.wireOp",EDGE,"E72.1");var subQ16=sQuery(id+"F12.wireOp",EDGE,"E74.1");var subQ18=sQuery(id+"F12.wireOp",EDGE,"E74.8");Q0=qUnion([makeQuery(id+"F12.imprint","IMPRINT",FACE,{"disambiguationData":[TD([[makeQuery(id+"F12.imprint","IMPRINT",EDGE,{"derivedFrom":subQ7}),1.0]])]}),makeQuery(id+"F12.imprint","IMPRINT",FACE,{"disambiguationData":[TD([[makeQuery(id+"F12.imprint","IMPRINT",EDGE,{"derivedFrom":subQ14}),1.0]])]}),makeQuery(id+"F12.imprint","IMPRINT",FACE,{"disambiguationData":[TD([[makeQuery(id+"F12.imprint","IMPRINT",EDGE,{"derivedFrom":subQ16}),1.0]])]}),makeQuery(id+"F12.imprint","IMPRINT",FACE,{"disambiguationData":[TD([[makeQuery(id+"F12.imprint","IMPRINT",EDGE,{"derivedFrom":subQ18}),-1.0]])]})]);}
            var Q1;
            Q1=makeQuery(id+"F5.boolean.opBoolean","SPLIT",FACE,{"disambiguationData":[TD([makeQuery(id+"F5.opExtrude","SWEPT_FACE",FACE,{"disambiguationData":[OSD([sQuery(id+"F4.wireOp",EDGE,"E41")])]})])],"derivedFrom":makeQuery(id+"F3.boolean.opBoolean","COPY",FACE,{"derivedFrom":makeQuery(id+"F3.opExtrude","CAP_FACE",FACE,{"disambiguationData":[OSD([sQuery(id+"F0.wireOp",EDGE,"E25.0"),sQuery(id+"F0.wireOp",EDGE,"E25.1"),sQuery(id+"F0.wireOp",EDGE,"E25.2"),sQuery(id+"F0.wireOp",EDGE,"E25.3"),sQuery(id+"F0.wireOp",EDGE,"E25.4"),sQuery(id+"F0.wireOp",EDGE,"E25.5"),sQuery(id+"F0.wireOp",EDGE,"E25.6"),sQuery(id+"F0.wireOp",EDGE,"E25.7")])],"isStart":false})})});
            extrude(context, id + "F13", {"entities" : qUnion([Q0]), "operationType" : NewBodyOperationType.REMOVE, "endBound" : BoundingType.UP_TO_SURFACE, "endBoundEntityFace" : qUnion([Q1]), "depth" : 25 * mm});
        }
        {
            var Q0;
            Q0=makeQuery(id+"F3.boolean.opBoolean","COPY",EDGE,{"derivedFrom":makeQuery(id+"F3.opExtrude","CAP_EDGE",EDGE,{"disambiguationData":[OSD([sQuery(id+"F0.wireOp",EDGE,"E25.6")])],"isStart":false})});
            var Q1;
            Q1=makeQuery(id+"F8.boolean.opBoolean","INTERSECT",EDGE,{"derivedFrom":[makeQuery(id+"F5.opExtrude","SWEPT_FACE",FACE,{"disambiguationData":[OSD([sQuery(id+"F4.wireOp",EDGE,"E30")])]}),makeQuery(id+"F8.opExtrude","CAP_FACE",FACE,{"disambiguationData":[OSD([sQuery(id+"F7.wireOp",EDGE,"E67")])],"isStart":false})]});
            var Q2;
            Q2=makeQuery(id+"F8.boolean.opBoolean","INTERSECT",EDGE,{"disambiguationData":[OD(1.0)],"derivedFrom":[makeQuery(id+"F5.opExtrude","SWEPT_FACE",FACE,{"disambiguationData":[OSD([sQuery(id+"F4.wireOp",EDGE,"E30")])]}),makeQuery(id+"F8.opExtrude","SWEPT_FACE",FACE,{"disambiguationData":[OSD([sQuery(id+"F7.wireOp",EDGE,"E67")])]})]});
            var Q3;
            {var subQ0=sQuery(id+"F4.wireOp",EDGE,"E30");Q3=makeQuery(id+"F8.boolean.opBoolean","SPLIT",EDGE,{"disambiguationData":[TD([makeQuery(id+"F5.opExtrude","SWEPT_FACE",FACE,{"disambiguationData":[OSD([sQuery(id+"F4.wireOp",EDGE,"E35.filletArc")])]})])],"derivedFrom":makeQuery(id+"F5.opExtrude","CAP_EDGE",EDGE,{"disambiguationData":[OSD([subQ0])],"isStart":false})});}
            var Q4;
            {var subQ0=sQuery(id+"F0.wireOp",EDGE,"E25.7");var subQ1=sQuery(id+"F0.wireOp",EDGE,"E25.1");var subQ2=sQuery(id+"F0.wireOp",EDGE,"E25.6");var subQ3=sQuery(id+"F0.wireOp",EDGE,"E25.5");var subQ4=sQuery(id+"F0.wireOp",EDGE,"E25.4");var subQ5=sQuery(id+"F0.wireOp",EDGE,"E25.0");var subQ6=sQuery(id+"F0.wireOp",EDGE,"E25.2");var subQ7=sQuery(id+"F0.wireOp",EDGE,"E25.3");Q4=makeQuery(id+"F8.boolean.opBoolean","INTERSECT",EDGE,{"derivedFrom":[makeQuery(id+"F5.boolean.opBoolean","SPLIT",FACE,{"disambiguationData":[TD([makeQuery(id+"F2.opExtrude","SWEPT_FACE",FACE,{"disambiguationData":[OSD([subQ5])]})])],"derivedFrom":makeQuery(id+"F3.boolean.opBoolean","COPY",FACE,{"derivedFrom":makeQuery(id+"F3.opExtrude","CAP_FACE",FACE,{"disambiguationData":[OSD([subQ5,subQ1,subQ6,subQ7,subQ4,subQ3,subQ2,subQ0])],"isStart":false})})}),makeQuery(id+"F8.opExtrude","SWEPT_FACE",FACE,{"disambiguationData":[OSD([sQuery(id+"F7.wireOp",EDGE,"E67")])]})]});}
            var Q5;
            Q5=makeQuery(id+"F8.boolean.opBoolean","INTERSECT",EDGE,{"disambiguationData":[OD(0.0)],"derivedFrom":[makeQuery(id+"F5.opExtrude","SWEPT_FACE",FACE,{"disambiguationData":[OSD([sQuery(id+"F4.wireOp",EDGE,"E30")])]}),makeQuery(id+"F8.opExtrude","SWEPT_FACE",FACE,{"disambiguationData":[OSD([sQuery(id+"F7.wireOp",EDGE,"E67")])]})]});
            fillet(context, id + "F14", {"entities" : qUnion([Q0, Q1, Q2, Q3, Q4, Q5]), "radius" : 3 * mm, "tangentPropagation" : true, "allowEdgeOverflow" : false});
        }
        {
            var Q0;
            Q0=makeQuery(id+"F1.opExtrude","CAP_EDGE",EDGE,{"disambiguationData":[OSD([sQuery(id+"F0.wireOp",EDGE,"E1.bottom")])],"isStart":false});
            fillet(context, id + "F15", {"entities" : qUnion([Q0]), "radius" : 2 * mm, "tangentPropagation" : true, "allowEdgeOverflow" : false});
        }
        {
            var Q0;
            {var subQ0=sQuery(id+"F0.wireOp",EDGE,"E21.filletArc");var subQ1=sQuery(id+"F0.wireOp",EDGE,"E7");var subQ2=sQuery(id+"F0.wireOp",EDGE,"E6");var subQ3=sQuery(id+"F0.wireOp",EDGE,"E5");var subQ4=sQuery(id+"F0.wireOp",EDGE,"E4");var subQ5=sQuery(id+"F0.wireOp",EDGE,"E22.filletArc");var subQ6=sQuery(id+"F0.wireOp",EDGE,"E1.bottom");var subQ7=sQuery(id+"F0.wireOp",EDGE,"E1.right");var subQ8=sQuery(id+"F0.wireOp",EDGE,"E1.top");var subQ9=sQuery(id+"F0.wireOp",EDGE,"E1.left");var subQ10=sQuery(id+"F0.wireOp",EDGE,"E23.filletArc");var subQ11=sQuery(id+"F0.wireOp",EDGE,"E24.filletArc");Q0=makeQuery(id+"F2.boolean.opBoolean","SPLIT",FACE,{"disambiguationData":[TD([makeQuery(id+"F1.opExtrude","SWEPT_FACE",FACE,{"disambiguationData":[OSD([subQ6])]})])],"derivedFrom":makeQuery(id+"F1.opExtrude","CAP_FACE",FACE,{"disambiguationData":[OSD([subQ6,subQ8,subQ9,subQ7,subQ4,subQ3,subQ2,subQ1,subQ0,subQ5,subQ10,subQ11])],"isStart":true})});}
            var sketch = newSketch(context, id + "F16", { "sketchPlane" : qUnion([Q0])});
            skSolve(sketch);
        }
        {
            var Q0;
            Q0=makeQuery(id+"F16.imprint","IMPRINT",FACE,{"disambiguationData":[TD([[makeQuery(id+"F16.imprint","IMPRINT",EDGE,{"derivedFrom":makeQuery(id+"F1.opExtrude","CAP_EDGE",EDGE,{"disambiguationData":[OSD([sQuery(id+"F0.wireOp",EDGE,"E1.bottom")])],"isStart":true})}),1.0]])]});
            var sketch = newSketch(context, id + "F17", { "sketchPlane" : qUnion([Q0])});
            skCircle(sketch, "E79", {"center": v(0, 120) * mm, "radius": 6 * mm});
            skLineSegment(sketch, "E80", {"start": v(-33, 90) * mm, "end": v(-15, 108) * mm});
            skLineSegment(sketch, "E81", {"start": v(33, 90) * mm, "end": v(15, 108) * mm});
            skLineSegment(sketch, "E82", {"start": v(-15, 108) * mm, "end": v(-15, 120) * mm});
            skLineSegment(sketch, "E83", {"start": v(15, 108) * mm, "end": v(15, 120) * mm});
            skArc(sketch, "E84", {"start": v(15, 120) * mm, "mid": v(0, 135) * mm, "end": v(-15, 120) * mm});
            skLineSegment(sketch, "E85", {"start": v(0, 120) * mm, "end": v(0, 90) * mm, "construction": true});
            skLineSegment(sketch, "E86", {"start": v(-80, 0) * mm, "end": v(80, 0) * mm, "construction": true});
            skCircle(sketch, "E87.MirrorC", {"center": v(0, -120) * mm, "radius": 6 * mm});
            skLineSegment(sketch, "E88.MirrorCS", {"start": v(-33, -90) * mm, "end": v(-15, -108) * mm});
            skLineSegment(sketch, "E89.MirrorCS", {"start": v(15, -108) * mm, "end": v(15, -120) * mm});
            skLineSegment(sketch, "E90.MirrorCS", {"start": v(33, -90) * mm, "end": v(15, -108) * mm});
            skLineSegment(sketch, "E91.MirrorCS", {"start": v(0, -120) * mm, "end": v(0, -90) * mm, "construction": true});
            skArc(sketch, "E92.MirrorCS", {"start": v(15, -120) * mm, "mid": v(0, -135) * mm, "end": v(-15, -120) * mm});
            skLineSegment(sketch, "E93.MirrorCS", {"start": v(-15, -108) * mm, "end": v(-15, -120) * mm});
            skSolve(sketch);
        }
        {
            var Q0;
            Q0=makeQuery(id+"F17.imprint","IMPRINT",FACE,{"disambiguationData":[TD([[makeQuery(id+"F17.imprint","IMPRINT",EDGE,{"derivedFrom":sQuery(id+"F17.wireOp",EDGE,"E79")}),-1.0]])]});
            var Q1;
            {var subQ1=sQuery(id+"F17.wireOp",EDGE,"E88.MirrorCS");Q1=makeQuery(id+"F17.imprint","IMPRINT",FACE,{"disambiguationData":[TD([[makeQuery(id+"F17.imprint","IMPRINT",EDGE,{"derivedFrom":subQ1}),1.0]])]});}
            var Q2;
            Q2=makeQuery(id+"F16.imprint","IMPRINT",FACE,{"disambiguationData":[TD([[makeQuery(id+"F16.imprint","IMPRINT",EDGE,{"derivedFrom":makeQuery(id+"F1.opExtrude","CAP_EDGE",EDGE,{"disambiguationData":[OSD([sQuery(id+"F0.wireOp",EDGE,"E1.bottom")])],"isStart":true})}),1.0]])]});
            var Q3;
            Q3=makeQuery(id+"F2.opExtrude","CAP_FACE",FACE,{"disambiguationData":[OSD([sQuery(id+"F0.wireOp",EDGE,"E12"),sQuery(id+"F0.wireOp",EDGE,"E13"),sQuery(id+"F0.wireOp",EDGE,"E14"),sQuery(id+"F0.wireOp",EDGE,"E15"),sQuery(id+"F0.wireOp",EDGE,"E17.filletArc"),sQuery(id+"F0.wireOp",EDGE,"E18.filletArc"),sQuery(id+"F0.wireOp",EDGE,"E19.filletArc"),sQuery(id+"F0.wireOp",EDGE,"E20.filletArc"),sQuery(id+"F0.wireOp",EDGE,"E25.0"),sQuery(id+"F0.wireOp",EDGE,"E25.1"),sQuery(id+"F0.wireOp",EDGE,"E25.2"),sQuery(id+"F0.wireOp",EDGE,"E25.3"),sQuery(id+"F0.wireOp",EDGE,"E25.4"),sQuery(id+"F0.wireOp",EDGE,"E25.5"),sQuery(id+"F0.wireOp",EDGE,"E25.6"),sQuery(id+"F0.wireOp",EDGE,"E25.7")])],"isStart":false});
            extrude(context, id + "F18", {"entities" : qUnion([Q0, Q1, Q2]), "endBound" : BoundingType.UP_TO_SURFACE, "endBoundEntityFace" : qUnion([Q3]), "depth" : 25 * mm});
        }
    });
